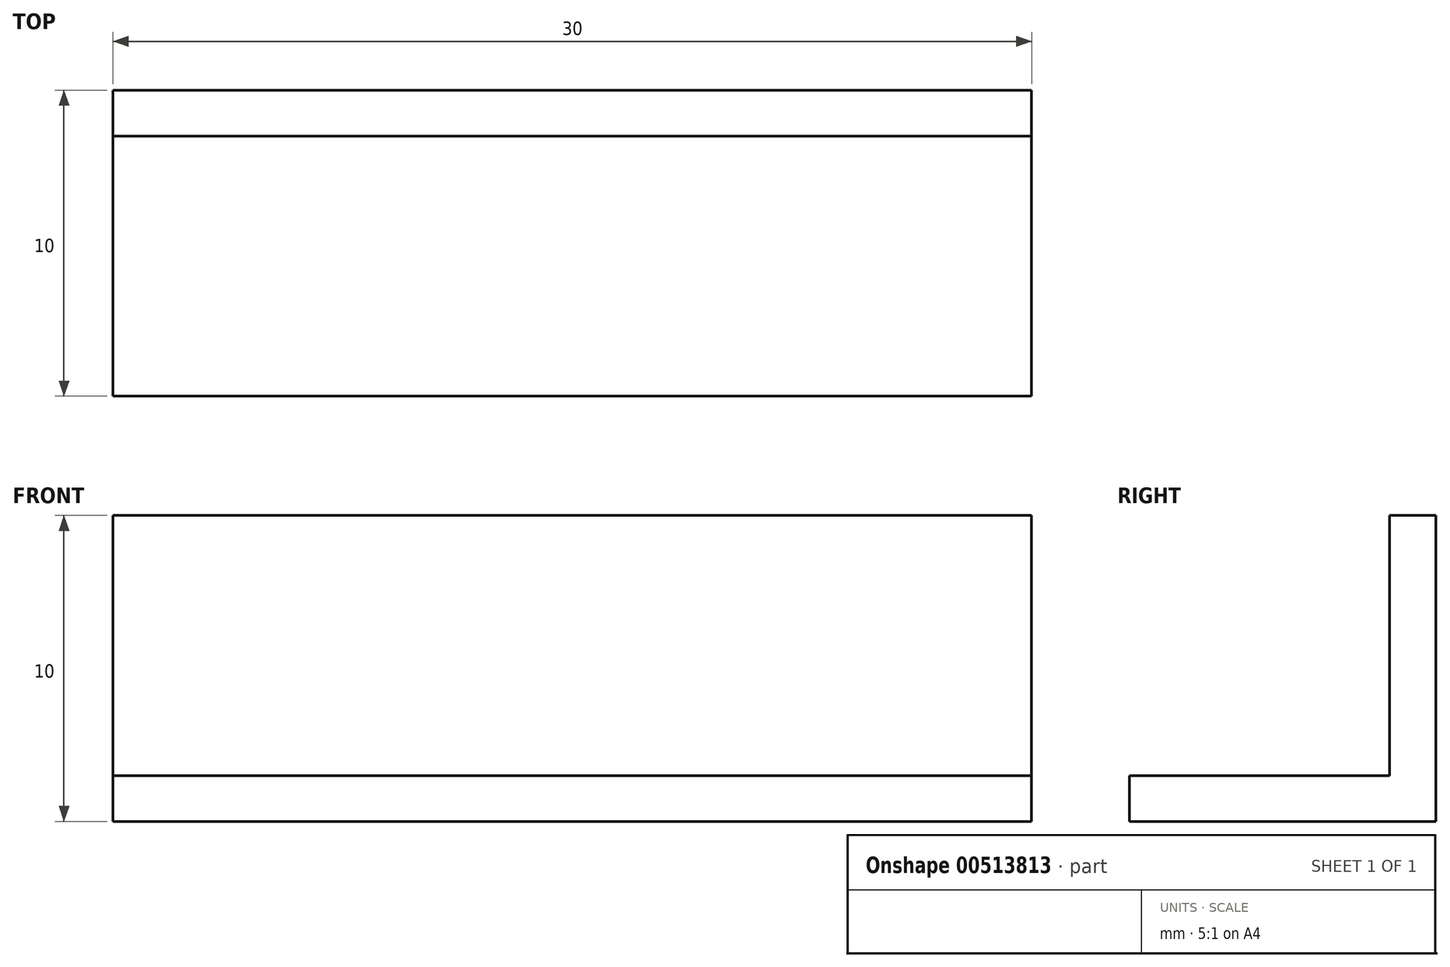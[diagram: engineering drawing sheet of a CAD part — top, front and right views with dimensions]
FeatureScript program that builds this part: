
annotation { "Feature Type Name" : "Feature", "Feature Type Description" : "" }
export const myFeature = defineFeature(function(context is Context, id is Id, definition is map)
    precondition{}
    {
        {
            var Q0;
            Q0=qCreatedBy(makeId("Top.planeOp"),FACE);
            var sketch = newSketch(context, id + "F0", { "sketchPlane" : qUnion([Q0])});
            skLineSegment(sketch, "E0.bottom", {"start": v(-8.07, 1.38) * mm, "end": v(21.93, 1.38) * mm});
            skLineSegment(sketch, "E0.top", {"start": v(-8.07, -8.62) * mm, "end": v(21.93, -8.62) * mm});
            skLineSegment(sketch, "E0.left", {"start": v(-8.07, 1.38) * mm, "end": v(-8.07, -8.62) * mm});
            skLineSegment(sketch, "E0.right", {"start": v(21.93, 1.38) * mm, "end": v(21.93, -8.62) * mm});
            skLineSegment(sketch, "E1.bottom", {"start": v(-8.07, -0.12) * mm, "end": v(21.93, -0.12) * mm});
            skLineSegment(sketch, "E2", {"start": v(-8.07, -0.12) * mm, "end": v(-8.07, 1.38) * mm});
            skSolve(sketch);
        }
        {
            var Q0;
            {var subQ0=sQuery(id+"F0.wireOp",EDGE,"E0.bottom");Q0=makeQuery(id+"F0.imprint","IMPRINT",FACE,{"disambiguationData":[TD([[makeQuery(id+"F0.imprint","IMPRINT",EDGE,{"derivedFrom":subQ0}),-1.0]])]});}
            var Q1;
            {var subQ0=sQuery(id+"F0.wireOp",EDGE,"E0.top");Q1=makeQuery(id+"F0.imprint","IMPRINT",FACE,{"disambiguationData":[TD([[makeQuery(id+"F0.imprint","IMPRINT",EDGE,{"derivedFrom":subQ0}),1.0]])]});}
            extrude(context, id + "F1", {"entities" : qUnion([Q0, Q1]), "depth" : 1.5 * mm, "offsetDistance" : 25 * mm});
        }
        {
            var Q0;
            {var subQ0=sQuery(id+"F0.wireOp",EDGE,"E0.bottom");Q0=makeQuery(id+"F0.imprint","IMPRINT",FACE,{"disambiguationData":[TD([[makeQuery(id+"F0.imprint","IMPRINT",EDGE,{"derivedFrom":subQ0}),-1.0]])]});}
            extrude(context, id + "F2", {"entities" : qUnion([Q0]), "operationType" : NewBodyOperationType.ADD, "depth" : 10 * mm, "offsetDistance" : 25 * mm});
        }
    });
